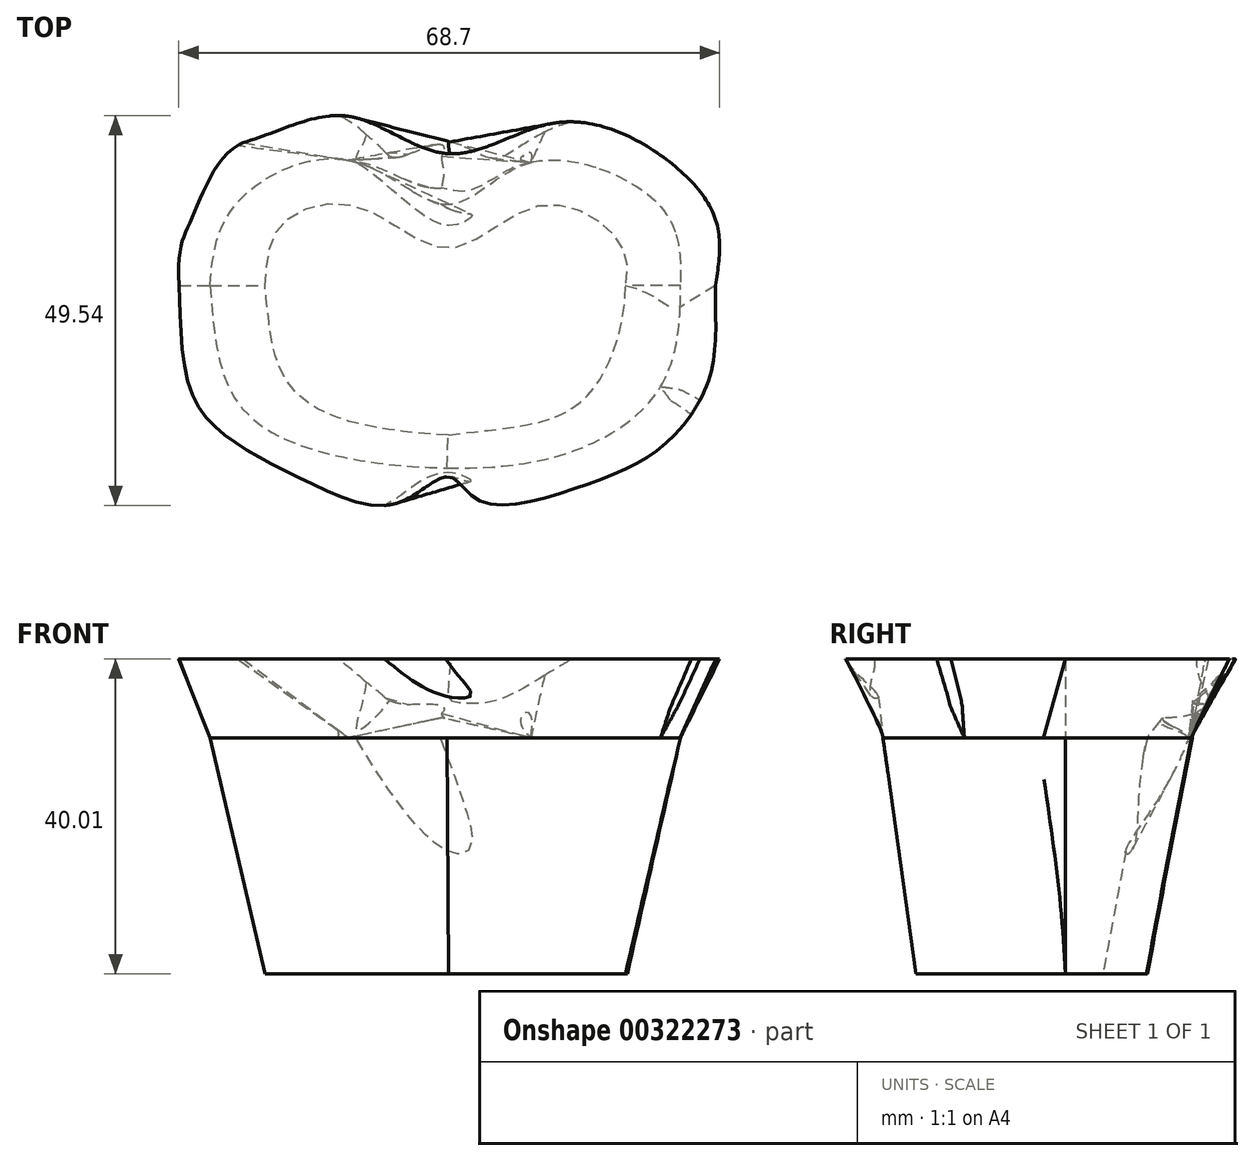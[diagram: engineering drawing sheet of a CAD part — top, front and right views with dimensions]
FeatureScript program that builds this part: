
annotation { "Feature Type Name" : "Feature", "Feature Type Description" : "" }
export const myFeature = defineFeature(function(context is Context, id is Id, definition is map)
    precondition{}
    {
        {
            var Q0;
            Q0=qCreatedBy(makeId("Top.planeOp"),FACE);
            var sketch = newSketch(context, id + "F0", { "sketchPlane" : qUnion([Q0])});
            skFitSpline(sketch, "E0", {"points": [v(-30.3, 0) * mm, v(-27.5, -13.68) * mm, v(-18.57, -20.39) * mm, v(0, -23.18) * mm, v(16.06, -20.94) * mm, v(26.95, -12.85) * mm, v(29.46, 0) * mm], "startDerivative": vector(7.19, -90.61) * mm, "endDerivative": vector(-1.38, 84.22) * mm});
            skFitSpline(sketch, "E1", {"points": [v(-30.3, 0) * mm, v(-27.23, 10.05) * mm, v(-12.7, 15.92) * mm, v(0, 10.33) * mm, v(10.47, 15.64) * mm, v(26.39, 10.61) * mm, v(29.46, 0) * mm], "startDerivative": vector(6.2, 69.74) * mm, "endDerivative": vector(-2.77, -91.11) * mm});
            skSolve(sketch);
        }
        {
            var Q0;
            Q0=qCreatedBy(makeId("Top.planeOp"),FACE);
            cPlane(context, id + "F1", {"entities" : qUnion([Q0]), "cplaneType" : CPlaneType.OFFSET, "offset" : 30 * mm, "oppositeDirection" : true, "width" : 150 * mm, "height" : 150 * mm});
        }
        {
            var Q0;
            Q0=qCreatedBy(id+"F1.planeOp",FACE);
            var sketch = newSketch(context, id + "F2", { "sketchPlane" : qUnion([Q0])});
            skFitSpline(sketch, "E2", {"points": [v(0, -18.99) * mm, v(-15.5, -16.2) * mm, v(-21.36, -10.61) * mm, v(-23.32, 0) * mm], "startDerivative": vector(-45.65, 2.41) * mm, "endDerivative": vector(-4.13, 36.61) * mm});
            skFitSpline(sketch, "E3", {"points": [v(0, -18.99) * mm, v(14.1, -16.48) * mm, v(20.25, -10.05) * mm, v(22.48, 0) * mm], "startDerivative": vector(36.72, 5.42) * mm, "endDerivative": vector(-0.15, 31.9) * mm});
            skFitSpline(sketch, "E4", {"points": [v(-23.32, 0) * mm, v(-21.36, 7.54) * mm, v(-11.59, 10.05) * mm, v(0, 4.75) * mm, v(11.03, 10.05) * mm, v(20.53, 6.98) * mm, v(22.48, 0) * mm], "startDerivative": vector(6.7, 55.03) * mm, "endDerivative": vector(-14.24, -57.87) * mm});
            skSolve(sketch);
        }
        {
            var Q0;
            Q0=makeQuery(id+"F0.imprint","IMPRINT",FACE,{"disambiguationData":[TD([[makeQuery(id+"F0.imprint","IMPRINT",EDGE,{"derivedFrom":sQuery(id+"F0.wireOp",EDGE,"E0")}),1.0]])]});
            var Q1;
            Q1=makeQuery(id+"F2.imprint","IMPRINT",FACE,{"disambiguationData":[TD([[makeQuery(id+"F2.imprint","IMPRINT",EDGE,{"derivedFrom":sQuery(id+"F2.wireOp",EDGE,"E2")}),-1.0]])]});
            loft(context, id + "F3", {"sheetProfilesArray" : [{ "sheetProfileEntities" : qUnion([Q0]) }, { "sheetProfileEntities" : qUnion([Q1]) }]});
        }
        {
            var Q1;
            Q1=makeQuery(id+"F3.opLoft","CAP_FACE",FACE,{"disambiguationData":[OSD([makeQuery(id+"F0.imprint","IMPRINT",FACE,{"disambiguationData":[TD([[makeQuery(id+"F0.imprint","IMPRINT",EDGE,{"derivedFrom":sQuery(id+"F0.wireOp",EDGE,"E0")}),1.0]])]})])],"isStart":true});
            var Q2;
            Q2=makeQuery(id+"F3.opLoft","MID_CAP_VERTEX",VERTEX,{"disambiguationData":[OSD([sQuery(id+"F2.wireOp",EDGE,"E3"),sQuery(id+"F2.wireOp",EDGE,"E4")])],"capPos":1.0});
            loft(context, id + "F4", {"operationType" : NewBodyOperationType.ADD, "sheetProfilesArray" : [{ "sheetProfileEntities" : qUnion([Q1]) }, { "sheetProfileEntities" : qUnion([Q2]) }]});
        }
        {
            var Q0;
            Q0=makeQuery(id+"F2.imprint","IMPRINT",FACE,{"disambiguationData":[TD([[makeQuery(id+"F2.imprint","IMPRINT",EDGE,{"derivedFrom":sQuery(id+"F2.wireOp",EDGE,"E2")}),-1.0]])]});
            extrude(context, id + "F5", {"entities" : qUnion([Q0]), "operationType" : NewBodyOperationType.ADD, "depth" : 25 * mm});
        }
        {
            var Q0;
            Q0=qCreatedBy(makeId("Top.planeOp"),FACE);
            cPlane(context, id + "F6", {"entities" : qUnion([Q0]), "cplaneType" : CPlaneType.OFFSET, "offset" : 10 * mm, "width" : 150 * mm, "height" : 150 * mm});
        }
        {
            var Q0;
            Q0=qCreatedBy(id+"F6.planeOp",FACE);
            var sketch = newSketch(context, id + "F7", { "sketchPlane" : qUnion([Q0])});
            skFitSpline(sketch, "E5", {"points": [v(-34.2, 0) * mm, v(-32.81, -13.13) * mm, v(-27.23, -19.83) * mm, v(-17.45, -25.13) * mm, v(-6.56, -27.65) * mm, v(0, -24.3) * mm, v(4.05, -27.37) * mm, v(17.17, -25.41) * mm, v(27.23, -20.39) * mm, v(33.37, -10.9) * mm, v(33.93, 0) * mm], "startDerivative": vector(5.02, -94.75) * mm, "endDerivative": vector(3.18, 93.59) * mm});
            skFitSpline(sketch, "E6", {"points": [v(33.93, 0) * mm, v(33.93, 8.38) * mm, v(26.67, 16.76) * mm, v(13.56, 20.66) * mm, v(0, 16.76) * mm, v(-12.7, 21.5) * mm, v(-26.1, 18.15) * mm], "startDerivative": vector(9.7, 63.44) * mm, "endDerivative": vector(-82.15, -23.59) * mm});
            skFitSpline(sketch, "E7", {"points": [v(-26.1, 18.15) * mm, v(-32.53, 8.66) * mm, v(-34.2, 0) * mm], "startDerivative": vector(-19.73, -8.57) * mm, "endDerivative": vector(1.79, -33.6) * mm});
            skSolve(sketch);
        }
        {
            var Q1;
            Q1=makeQuery(id+"F7.imprint","IMPRINT",FACE,{"disambiguationData":[TD([[makeQuery(id+"F7.imprint","IMPRINT",EDGE,{"derivedFrom":sQuery(id+"F7.wireOp",EDGE,"E5")}),1.0]])]});
            var Q2;
            Q2=makeQuery(id+"F3.opLoft","CAP_FACE",FACE,{"disambiguationData":[OSD([makeQuery(id+"F0.imprint","IMPRINT",FACE,{"disambiguationData":[TD([[makeQuery(id+"F0.imprint","IMPRINT",EDGE,{"derivedFrom":sQuery(id+"F0.wireOp",EDGE,"E0")}),1.0]])]})])],"isStart":true});
            loft(context, id + "F8", {"operationType" : NewBodyOperationType.ADD, "sheetProfilesArray" : [{ "sheetProfileEntities" : qUnion([Q1]) }, { "sheetProfileEntities" : qUnion([Q2]) }]});
        }
        {
            var Q0;
            Q0=makeQuery(id+"F0.imprint","IMPRINT",FACE,{"disambiguationData":[TD([[makeQuery(id+"F0.imprint","IMPRINT",EDGE,{"derivedFrom":sQuery(id+"F0.wireOp",EDGE,"E0")}),1.0]])]});
            extrude(context, id + "F9", {"entities" : qUnion([Q0]), "operationType" : NewBodyOperationType.ADD, "depth" : 10 * mm});
        }
        {
            var Q1;
            Q1=makeQuery(id+"F8.opLoft","CAP_FACE",FACE,{"disambiguationData":[OSD([makeQuery(id+"F7.imprint","IMPRINT",FACE,{"disambiguationData":[TD([[makeQuery(id+"F7.imprint","IMPRINT",EDGE,{"derivedFrom":sQuery(id+"F7.wireOp",EDGE,"E5")}),1.0]])]})])],"isStart":true});
            var Q2;
            Q2=sQuery(id+"F0.wireOp",VERTEX,"E1.4.internal");
            loft(context, id + "F10", {"operationType" : NewBodyOperationType.ADD, "sheetProfilesArray" : [{ "sheetProfileEntities" : qUnion([Q1]) }, { "sheetProfileEntities" : qUnion([Q2]) }]});
        }
        {
            var Q1;
            Q1=makeQuery(id+"F8.opLoft","CAP_FACE",FACE,{"disambiguationData":[OSD([makeQuery(id+"F7.imprint","IMPRINT",FACE,{"disambiguationData":[TD([[makeQuery(id+"F7.imprint","IMPRINT",EDGE,{"derivedFrom":sQuery(id+"F7.wireOp",EDGE,"E5")}),1.0]])]})])],"isStart":true});
            var Q2;
            Q2=sQuery(id+"F0.wireOp",VERTEX,"E1.2.internal");
            loft(context, id + "F11", {"operationType" : NewBodyOperationType.ADD, "sheetProfilesArray" : [{ "sheetProfileEntities" : qUnion([Q1]) }, { "sheetProfileEntities" : qUnion([Q2]) }]});
        }
        {
            var Q0;
            Q0=qCreatedBy(id+"F6.planeOp",FACE);
            cPlane(context, id + "F12", {"entities" : qUnion([Q0]), "cplaneType" : CPlaneType.OFFSET, "offset" : 25 * mm, "width" : 150 * mm, "height" : 150 * mm});
        }
        {
            var Q1;
            Q1=makeQuery(id+"F7.imprint","IMPRINT",FACE,{"disambiguationData":[TD([[makeQuery(id+"F7.imprint","IMPRINT",EDGE,{"derivedFrom":sQuery(id+"F7.wireOp",EDGE,"E5")}),1.0]])]});
            var Q2;
            Q2=sQuery(id+"F0.wireOp",VERTEX,"E0.5.internal");
            loft(context, id + "F13", {"operationType" : NewBodyOperationType.ADD, "sheetProfilesArray" : [{ "sheetProfileEntities" : qUnion([Q1]) }, { "sheetProfileEntities" : qUnion([Q2]) }]});
        }
        {
            var Q1;
            Q1=makeQuery(id+"F7.imprint","IMPRINT",FACE,{"disambiguationData":[TD([[makeQuery(id+"F7.imprint","IMPRINT",EDGE,{"derivedFrom":sQuery(id+"F7.wireOp",EDGE,"E5")}),1.0]])]});
            var Q2;
            Q2=sQuery(id+"F0.wireOp",VERTEX,"E0.4.internal");
            loft(context, id + "F14", {"operationType" : NewBodyOperationType.ADD, "sheetProfilesArray" : [{ "sheetProfileEntities" : qUnion([Q1]) }, { "sheetProfileEntities" : qUnion([Q2]) }]});
        }
    });
